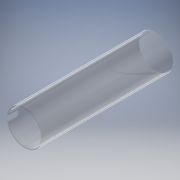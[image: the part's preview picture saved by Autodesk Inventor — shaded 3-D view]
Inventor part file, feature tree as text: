
AUTODESK INVENTOR PART (.ipt)
format: ipt  version: 2016 (Build 200138000, 138)  size: 120,320 bytes
history: native  units: mm
features: reference x3, extrude x2, sketch x2
ambient origin geometry x8: Origin, YZ Plane, XZ Plane, XY Plane, X Axis, Y Axis, Z Axis, Center Point
bodies: Solid1 (feature_tree)
feature tree (7):
  extrude  "Extrusion1"  Depth=3.5mm
  extrude  "Extrusion2"  Depth=400.0mm TaperAngle=0.0deg
  sketch  "Sketch1"  dims[d0=100.0mm d1=3.5mm]
  sketch  "Sketch3"  dims[d2=400.0mm d3=0.0mm d4=400.0mm d5=0.0mm]
  reference  "Reference2"
  reference  "Reference3"
  reference  "Reference4"
